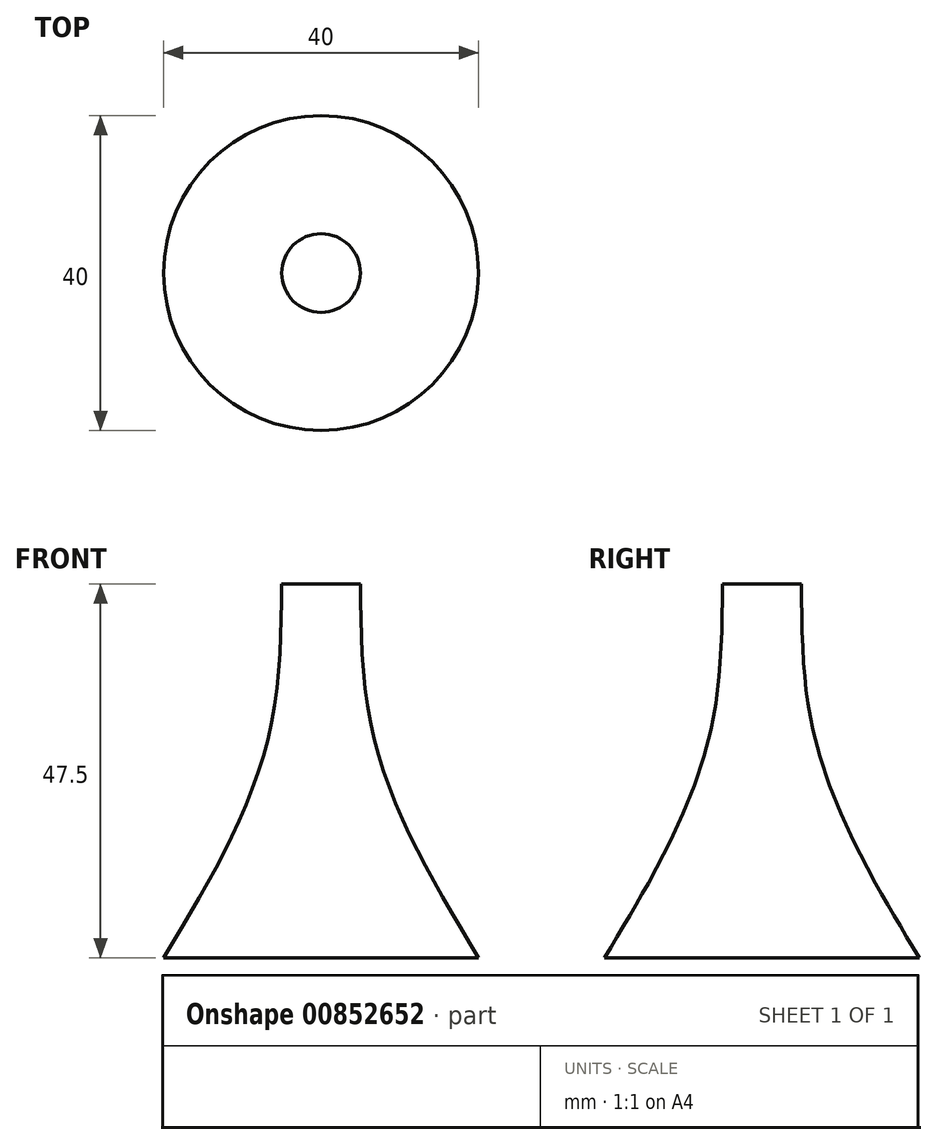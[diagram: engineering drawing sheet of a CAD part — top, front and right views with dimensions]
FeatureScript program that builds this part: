
annotation { "Feature Type Name" : "Feature", "Feature Type Description" : "" }
export const myFeature = defineFeature(function(context is Context, id is Id, definition is map)
    precondition{}
    {
        {
            var Q0;
            Q0=qCreatedBy(makeId("Top.planeOp"),FACE);
            var sketch = newSketch(context, id + "F0", { "sketchPlane" : qUnion([Q0])});
            skCircle(sketch, "E0", {"center": v(0, 0) * mm, "radius": 20 * mm});
            skSolve(sketch);
        }
        {
            var Q0;
            Q0=qCreatedBy(makeId("Top.planeOp"),FACE);
            cPlane(context, id + "F1", {"entities" : qUnion([Q0]), "cplaneType" : CPlaneType.OFFSET, "offset" : 30 * mm, "width" : 152.4 * mm, "height" : 152.4 * mm});
        }
        {
            var Q0;
            Q0=qCreatedBy(id+"F1.planeOp",FACE);
            var sketch = newSketch(context, id + "F2", { "sketchPlane" : qUnion([Q0])});
            skCircle(sketch, "E1", {"center": v(0, 0) * mm, "radius": 6.25 * mm});
            skSolve(sketch);
        }
        {
            var Q0;
            Q0=qCreatedBy(makeId("Top.planeOp"),FACE);
            cPlane(context, id + "F3", {"entities" : qUnion([Q0]), "cplaneType" : CPlaneType.OFFSET, "offset" : 47.5 * mm, "width" : 152.4 * mm, "height" : 152.4 * mm});
        }
        {
            var Q0;
            Q0=qCreatedBy(id+"F3.planeOp",FACE);
            var sketch = newSketch(context, id + "F4", { "sketchPlane" : qUnion([Q0])});
            skCircle(sketch, "E2", {"center": v(0, 0) * mm, "radius": 5 * mm});
            skSolve(sketch);
        }
        {
            var Q0;
            Q0=makeQuery(id+"F0.imprint","IMPRINT",FACE,{"disambiguationData":[TD([[makeQuery(id+"F0.imprint","IMPRINT",EDGE,{"derivedFrom":sQuery(id+"F0.wireOp",EDGE,"E0")}),1.0]])]});
            var Q1;
            Q1=makeQuery(id+"F2.imprint","IMPRINT",FACE,{"disambiguationData":[TD([[makeQuery(id+"F2.imprint","IMPRINT",EDGE,{"derivedFrom":sQuery(id+"F2.wireOp",EDGE,"E1")}),1.0]])]});
            var Q2;
            Q2=makeQuery(id+"F4.imprint","IMPRINT",FACE,{"disambiguationData":[TD([[makeQuery(id+"F4.imprint","IMPRINT",EDGE,{"derivedFrom":sQuery(id+"F4.wireOp",EDGE,"E2")}),1.0]])]});
            loft(context, id + "F5", {"sheetProfilesArray" : [{ "sheetProfileEntities" : qUnion([Q0]) }, { "sheetProfileEntities" : qUnion([Q1]) }, { "sheetProfileEntities" : qUnion([Q2]) }]});
        }
    });
